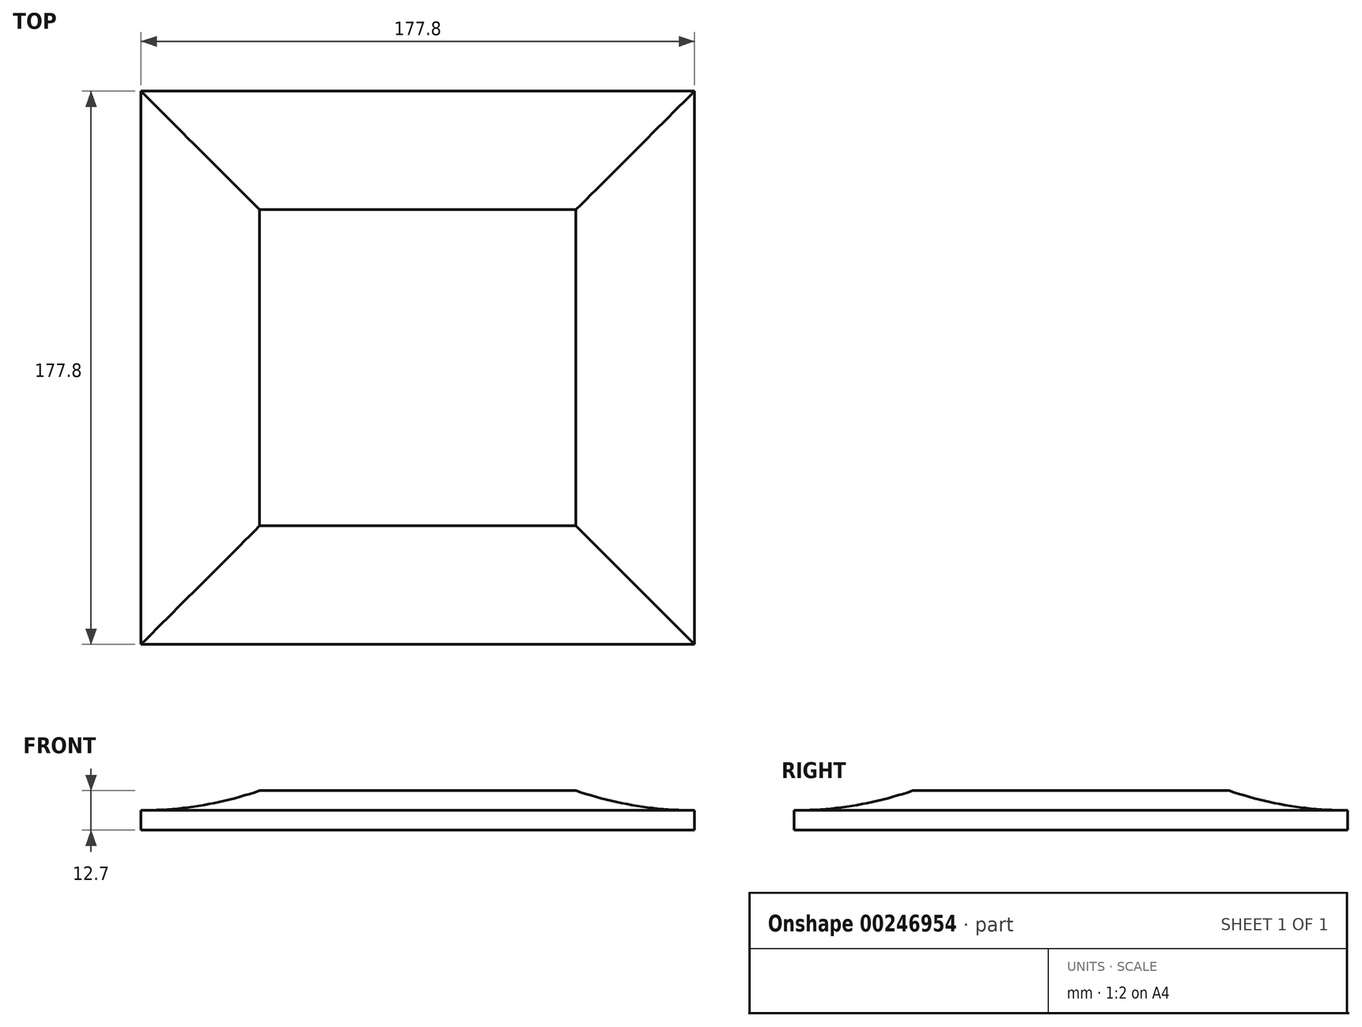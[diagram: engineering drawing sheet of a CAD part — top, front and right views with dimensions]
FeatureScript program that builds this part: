
annotation { "Feature Type Name" : "Feature", "Feature Type Description" : "" }
export const myFeature = defineFeature(function(context is Context, id is Id, definition is map)
    precondition{}
    {
        {
            var Q0;
            Q0=qCreatedBy(makeId("Top.planeOp"),FACE);
            var sketch = newSketch(context, id + "F0", { "sketchPlane" : qUnion([Q0])});
            skLineSegment(sketch, "E0.bottom", {"start": v(88.9, -88.9) * mm, "end": v(-88.9, -88.9) * mm});
            skLineSegment(sketch, "E0.top", {"start": v(88.9, 88.9) * mm, "end": v(-88.9, 88.9) * mm});
            skLineSegment(sketch, "E0.left", {"start": v(88.9, -88.9) * mm, "end": v(88.9, 88.9) * mm});
            skLineSegment(sketch, "E0.right", {"start": v(-88.9, -88.9) * mm, "end": v(-88.9, 88.9) * mm});
            skPoint(sketch, "E0.middle", {"position": v(0, 0) * mm});
            skSolve(sketch);
        }
        {
            var Q0;
            Q0=qCreatedBy(makeId("Front.planeOp"),FACE);
            var sketch = newSketch(context, id + "F1", { "sketchPlane" : qUnion([Q0])});
            skPoint(sketch, "E1.0", {"position": v(88.9, 0) * mm});
            skLineSegment(sketch, "E2", {"start": v(0, 0) * mm, "end": v(88.9, 0) * mm});
            skLineSegment(sketch, "E3", {"start": v(88.9, 0) * mm, "end": v(88.9, 6.35) * mm});
            skLineSegment(sketch, "E4", {"start": v(88.9, 6.35) * mm, "end": v(116.23, 6.35) * mm, "construction": true});
            skLineSegment(sketch, "E5", {"start": v(0, 0) * mm, "end": v(0, 12.7) * mm});
            skLineSegment(sketch, "E6", {"start": v(0, 12.7) * mm, "end": v(50.8, 12.7) * mm});
            skArc(sketch, "E7", {"start": v(88.9, 6.35) * mm, "mid": v(69.59, 7.95) * mm, "end": v(50.8, 12.7) * mm});
            skSolve(sketch);
        }
        {
            var Q0;
            Q0=makeQuery(id+"F1.imprint","IMPRINT",FACE,{"disambiguationData":[TD([[makeQuery(id+"F1.imprint","IMPRINT",EDGE,{"derivedFrom":sQuery(id+"F1.wireOp",EDGE,"E2")}),1.0]])]});
            var Q1;
            Q1 = qConstructionFilter(qBodyType(qCreatedBy(id + "F0" ,EDGE), BodyType.WIRE), ConstructionObject.NO);
            sweep(context, id + "F2", {"profiles" : qUnion([Q0]), "path" : qUnion([Q1])});
        }
    });
